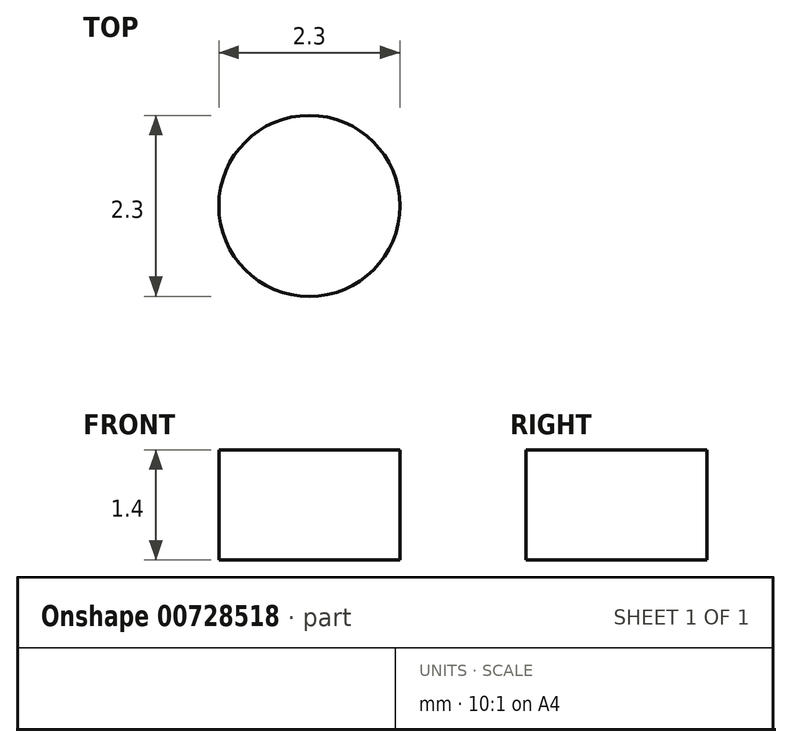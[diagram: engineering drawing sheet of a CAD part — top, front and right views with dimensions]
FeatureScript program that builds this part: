
annotation { "Feature Type Name" : "Feature", "Feature Type Description" : "" }
export const myFeature = defineFeature(function(context is Context, id is Id, definition is map)
    precondition{}
    {
        {
            var Q0;
            Q0=qCreatedBy(makeId("Top.planeOp"),FACE);
            var sketch = newSketch(context, id + "F0", { "sketchPlane" : qUnion([Q0])});
            skCircle(sketch, "E0", {"center": v(0, 0) * mm, "radius": 1.15 * mm});
            skSolve(sketch);
        }
        {
            var Q0;
            Q0=qSketchRegion(id+"F0",true);
            extrude(context, id + "F1", {"entities" : qUnion([Q0]), "depth" : 1.4 * mm, "offsetDistance" : 25 * mm});
        }
    });
